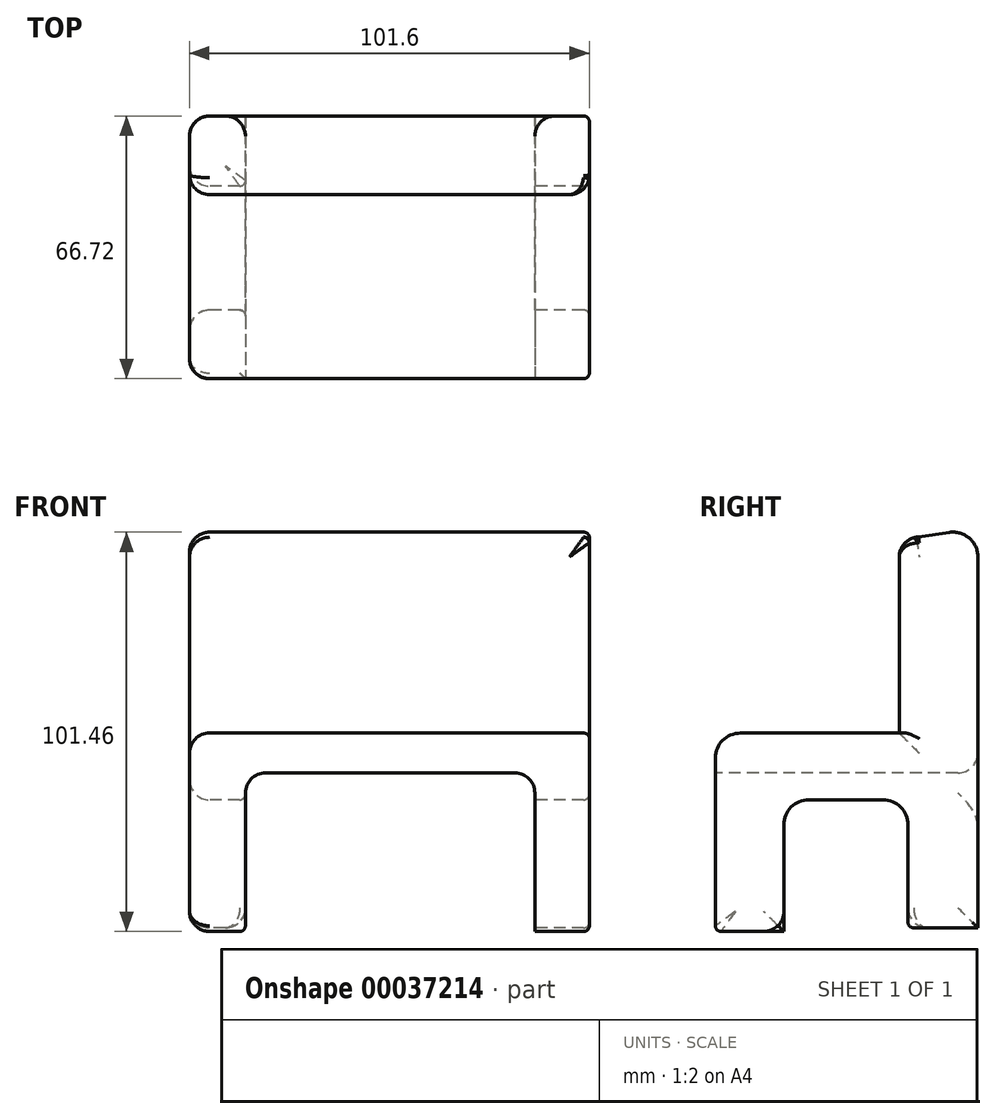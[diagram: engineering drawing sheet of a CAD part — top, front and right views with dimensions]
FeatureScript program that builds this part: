
annotation { "Feature Type Name" : "Feature", "Feature Type Description" : "" }
export const myFeature = defineFeature(function(context is Context, id is Id, definition is map)
    precondition{}
    {
        {
            var Q0;
            Q0=qCreatedBy(makeId("Right.planeOp"),FACE);
            var sketch = newSketch(context, id + "F0", { "sketchPlane" : qUnion([Q0])});
            skLineSegment(sketch, "E0", {"start": v(55.36, 61.66) * mm, "end": v(55.36, 14.39) * mm});
            skLineSegment(sketch, "E1", {"start": v(55.36, 14.39) * mm, "end": v(55.36, -32.54) * mm});
            skLineSegment(sketch, "E2", {"start": v(55.36, -32.54) * mm, "end": v(37.58, -32.54) * mm});
            skLineSegment(sketch, "E3", {"start": v(37.58, -32.54) * mm, "end": v(37.58, -6.35) * mm});
            skLineSegment(sketch, "E4", {"start": v(31.23, 0) * mm, "end": v(12.4, 0) * mm});
            skLineSegment(sketch, "E5", {"start": v(6.05, -6.35) * mm, "end": v(6.05, -33.45) * mm});
            skLineSegment(sketch, "E6", {"start": v(6.05, -33.45) * mm, "end": v(-11.36, -33.45) * mm});
            skLineSegment(sketch, "E7", {"start": v(-11.36, -33.45) * mm, "end": v(-11.36, 0) * mm});
            skLineSegment(sketch, "E8", {"start": v(-11.36, 0) * mm, "end": v(-11.36, 10.6) * mm});
            skLineSegment(sketch, "E9", {"start": v(-5.01, 16.96) * mm, "end": v(35.38, 16.96) * mm});
            skLineSegment(sketch, "E10", {"start": v(35.38, 16.96) * mm, "end": v(35.38, 66.08) * mm});
            skLineSegment(sketch, "E11", {"start": v(35.38, 66.08) * mm, "end": v(48.08, 67.94) * mm});
            skPoint(sketch, "E12.visualSharp", {"position": v(55.36, 69.01) * mm});
            skArc(sketch, "E12.filletArc", {"start": v(55.36, 61.66) * mm, "mid": v(53.16, 66.47) * mm, "end": v(48.08, 67.94) * mm});
            skPoint(sketch, "E13.visualSharp", {"position": v(-11.36, 16.96) * mm});
            skArc(sketch, "E13.filletArc", {"start": v(-5.01, 16.96) * mm, "mid": v(-9.5, 15.1) * mm, "end": v(-11.36, 10.6) * mm});
            skPoint(sketch, "E14.visualSharp", {"position": v(6.05, 0) * mm});
            skArc(sketch, "E14.filletArc", {"start": v(12.4, 0) * mm, "mid": v(7.9, -1.86) * mm, "end": v(6.05, -6.35) * mm});
            skPoint(sketch, "E15.visualSharp", {"position": v(37.58, 0) * mm});
            skArc(sketch, "E15.filletArc", {"start": v(37.58, -6.35) * mm, "mid": v(35.72, -1.86) * mm, "end": v(31.23, 0) * mm});
            skSolve(sketch);
        }
        {
            var Q0;
            Q0=makeQuery(id+"F0.imprint","IMPRINT",FACE,{"disambiguationData":[TD([[makeQuery(id+"F0.imprint","IMPRINT",EDGE,{"derivedFrom":sQuery(id+"F0.wireOp",EDGE,"E0")}),-1.0]])]});
            extrude(context, id + "F1", {"entities" : qUnion([Q0]), "depth" : 101.6 * mm});
        }
        {
            var Q0;
            Q0=makeQuery(id+"F1.opExtrude","SWEPT_FACE",FACE,{"disambiguationData":[OSD([sQuery(id+"F0.wireOp",EDGE,"E7"),sQuery(id+"F0.wireOp",EDGE,"E8")])]});
            var sketch = newSketch(context, id + "F2", { "sketchPlane" : qUnion([Q0])});
            skLineSegment(sketch, "E16.bottom", {"start": v(14.22, 6.83) * mm, "end": v(87.74, 6.83) * mm});
            skLineSegment(sketch, "E16.top", {"start": v(14.22, -33.45) * mm, "end": v(87.74, -33.45) * mm});
            skLineSegment(sketch, "E16.left", {"start": v(14.22, 6.83) * mm, "end": v(14.22, -33.45) * mm});
            skLineSegment(sketch, "E16.right", {"start": v(87.74, 6.83) * mm, "end": v(87.74, -33.45) * mm});
            skSolve(sketch);
        }
        {
            var Q0;
            Q0=makeQuery(id+"F2.imprint","IMPRINT",FACE,{"disambiguationData":[TD([[makeQuery(id+"F2.imprint","IMPRINT",EDGE,{"derivedFrom":sQuery(id+"F2.wireOp",EDGE,"E16.bottom")}),-1.0]])]});
            extrude(context, id + "F3", {"entities" : qUnion([Q0]), "operationType" : NewBodyOperationType.REMOVE, "oppositeDirection" : true, "depth" : 101.6 * mm});
        }
        {
            var Q0;
            Q0=makeQuery(id+"F1.opExtrude","CAP_FACE",FACE,{"disambiguationData":[OSD([sQuery(id+"F0.wireOp",EDGE,"E0"),sQuery(id+"F0.wireOp",EDGE,"E1"),sQuery(id+"F0.wireOp",EDGE,"E2"),sQuery(id+"F0.wireOp",EDGE,"E3"),sQuery(id+"F0.wireOp",EDGE,"E4"),sQuery(id+"F0.wireOp",EDGE,"E5"),sQuery(id+"F0.wireOp",EDGE,"E6"),sQuery(id+"F0.wireOp",EDGE,"E7"),sQuery(id+"F0.wireOp",EDGE,"E8"),sQuery(id+"F0.wireOp",EDGE,"E9"),sQuery(id+"F0.wireOp",EDGE,"E10"),sQuery(id+"F0.wireOp",EDGE,"E11"),sQuery(id+"F0.wireOp",EDGE,"E12.filletArc"),sQuery(id+"F0.wireOp",EDGE,"E13.filletArc"),sQuery(id+"F0.wireOp",EDGE,"E14.filletArc"),sQuery(id+"F0.wireOp",EDGE,"E15.filletArc")])],"isStart":true});
            fillet(context, id + "F4", {"entities" : qUnion([Q0]), "radius" : 5.08 * mm, "tangentPropagation" : true, "allowEdgeOverflow" : false});
        }
        {
            var Q0;
            Q0=makeQuery(id+"F3.boolean.opBoolean","COPY",EDGE,{"derivedFrom":makeQuery(id+"F3.opExtrude","CAP_EDGE",EDGE,{"disambiguationData":[OSD([sQuery(id+"F2.wireOp",EDGE,"E16.left")])],"isStart":true})});
            var Q1;
            Q1=makeQuery(id+"F3.boolean.opBoolean","COPY",EDGE,{"derivedFrom":makeQuery(id+"F3.opExtrude","CAP_EDGE",EDGE,{"disambiguationData":[OSD([sQuery(id+"F2.wireOp",EDGE,"E16.bottom")])],"isStart":true})});
            var Q2;
            Q2=makeQuery(id+"F3.boolean.opBoolean","INTERSECT",EDGE,{"derivedFrom":[makeQuery(id+"F1.opExtrude","SWEPT_FACE",FACE,{"disambiguationData":[OSD([sQuery(id+"F0.wireOp",EDGE,"E5")])]}),makeQuery(id+"F3.opExtrude","SWEPT_FACE",FACE,{"disambiguationData":[OSD([sQuery(id+"F2.wireOp",EDGE,"E16.left")])]})]});
            var Q3;
            Q3=makeQuery(id+"F3.boolean.opBoolean","COPY",EDGE,{"derivedFrom":makeQuery(id+"F3.opExtrude","SWEPT_EDGE",EDGE,{"disambiguationData":[OSD([sQuery(id+"F0.wireOp",EDGE,"E6"),sQuery(id+"F0.wireOp",EDGE,"E7"),sQuery(id+"F2.wireOp",EDGE,"E16.top"),sQuery(id+"F2.wireOp",EDGE,"E16.left")])]})});
            var Q4;
            {var subQ0=sQuery(id+"F0.wireOp",EDGE,"E6");var subQ1=sQuery(id+"F0.wireOp",EDGE,"E7");Q4=makeQuery(id+"F3.boolean.opBoolean","SPLIT",EDGE,{"disambiguationData":[TD([makeQuery(id+"F3.opExtrude","SWEPT_FACE",FACE,{"disambiguationData":[OSD([sQuery(id+"F2.wireOp",EDGE,"E16.left")])]})])],"derivedFrom":makeQuery(id+"F1.opExtrude","SWEPT_EDGE",EDGE,{"disambiguationData":[OSD([subQ0,subQ1])]})});}
            var Q5;
            {var subQ0=sQuery(id+"F0.wireOp",EDGE,"E6");var subQ1=sQuery(id+"F0.wireOp",EDGE,"E7");Q5=makeQuery(id+"F3.boolean.opBoolean","SPLIT",EDGE,{"disambiguationData":[TD([makeQuery(id+"F3.opExtrude","SWEPT_FACE",FACE,{"disambiguationData":[OSD([sQuery(id+"F2.wireOp",EDGE,"E16.right")])]})])],"derivedFrom":makeQuery(id+"F1.opExtrude","SWEPT_EDGE",EDGE,{"disambiguationData":[OSD([subQ0,subQ1])]})});}
            var Q6;
            Q6=makeQuery(id+"F1.opExtrude","CAP_EDGE",EDGE,{"disambiguationData":[OSD([sQuery(id+"F0.wireOp",EDGE,"E6")])],"isStart":false});
            var Q7;
            Q7=makeQuery(id+"F1.opExtrude","CAP_EDGE",EDGE,{"disambiguationData":[OSD([sQuery(id+"F0.wireOp",EDGE,"E7"),sQuery(id+"F0.wireOp",EDGE,"E8")])],"isStart":false});
            var Q8;
            Q8=makeQuery(id+"F3.boolean.opBoolean","COPY",EDGE,{"derivedFrom":makeQuery(id+"F3.opExtrude","CAP_EDGE",EDGE,{"disambiguationData":[OSD([sQuery(id+"F2.wireOp",EDGE,"E16.right")])],"isStart":true})});
            var Q9;
            Q9=makeQuery(id+"F1.opExtrude","CAP_EDGE",EDGE,{"disambiguationData":[OSD([sQuery(id+"F0.wireOp",EDGE,"E14.filletArc")])],"isStart":false});
            var Q10;
            Q10=makeQuery(id+"F1.opExtrude","CAP_EDGE",EDGE,{"disambiguationData":[OSD([sQuery(id+"F0.wireOp",EDGE,"E5")])],"isStart":false});
            var Q11;
            Q11=makeQuery(id+"F1.opExtrude","CAP_EDGE",EDGE,{"disambiguationData":[OSD([sQuery(id+"F0.wireOp",EDGE,"E4")])],"isStart":false});
            var Q12;
            Q12=makeQuery(id+"F1.opExtrude","CAP_EDGE",EDGE,{"disambiguationData":[OSD([sQuery(id+"F0.wireOp",EDGE,"E15.filletArc")])],"isStart":false});
            var Q13;
            Q13=makeQuery(id+"F1.opExtrude","CAP_EDGE",EDGE,{"disambiguationData":[OSD([sQuery(id+"F0.wireOp",EDGE,"E3")])],"isStart":false});
            var Q14;
            Q14=makeQuery(id+"F1.opExtrude","CAP_EDGE",EDGE,{"disambiguationData":[OSD([sQuery(id+"F0.wireOp",EDGE,"E2")])],"isStart":false});
            var Q15;
            {var subQ0=sQuery(id+"F0.wireOp",EDGE,"E2");var subQ1=sQuery(id+"F0.wireOp",EDGE,"E3");Q15=makeQuery(id+"F3.boolean.opBoolean","SPLIT",EDGE,{"disambiguationData":[TD([makeQuery(id+"F3.opExtrude","SWEPT_FACE",FACE,{"disambiguationData":[OSD([sQuery(id+"F2.wireOp",EDGE,"E16.right")])]})])],"derivedFrom":makeQuery(id+"F1.opExtrude","SWEPT_EDGE",EDGE,{"disambiguationData":[OSD([subQ0,subQ1])]})});}
            var Q16;
            Q16=makeQuery(id+"F1.opExtrude","CAP_EDGE",EDGE,{"disambiguationData":[OSD([sQuery(id+"F0.wireOp",EDGE,"E0"),sQuery(id+"F0.wireOp",EDGE,"E1")])],"isStart":false});
            fillet(context, id + "F5", {"entities" : qUnion([Q0, Q1, Q2, Q3, Q4, Q5, Q6, Q7, Q8, Q9, Q10, Q11, Q12, Q13, Q14, Q15, Q16]), "radius" : 1.45 * mm, "tangentPropagation" : true, "allowEdgeOverflow" : false});
        }
        {
            var Q0;
            Q0=makeQuery(id+"F1.opExtrude","CAP_EDGE",EDGE,{"disambiguationData":[OSD([sQuery(id+"F0.wireOp",EDGE,"E10")])],"isStart":false});
            var Q1;
            Q1=makeQuery(id+"F1.opExtrude","SWEPT_EDGE",EDGE,{"disambiguationData":[OSD([sQuery(id+"F0.wireOp",EDGE,"E10"),sQuery(id+"F0.wireOp",EDGE,"E11")])]});
            var Q2;
            {var subQ0=sQuery(id+"F0.wireOp",EDGE,"E6");Q2=makeQuery(id+"F5.opFillet","BLEND_EDGE",EDGE,{"blendedFrom":[makeQuery(id+"F1.opExtrude","CAP_EDGE",EDGE,{"disambiguationData":[OSD([subQ0])],"isStart":false}),makeQuery(id+"F1.opExtrude","CAP_FACE",FACE,{"disambiguationData":[OSD([sQuery(id+"F0.wireOp",EDGE,"E0"),sQuery(id+"F0.wireOp",EDGE,"E1"),sQuery(id+"F0.wireOp",EDGE,"E2"),sQuery(id+"F0.wireOp",EDGE,"E3"),sQuery(id+"F0.wireOp",EDGE,"E4"),sQuery(id+"F0.wireOp",EDGE,"E5"),subQ0,sQuery(id+"F0.wireOp",EDGE,"E7"),sQuery(id+"F0.wireOp",EDGE,"E8"),sQuery(id+"F0.wireOp",EDGE,"E9"),sQuery(id+"F0.wireOp",EDGE,"E10"),sQuery(id+"F0.wireOp",EDGE,"E11"),sQuery(id+"F0.wireOp",EDGE,"E12.filletArc"),sQuery(id+"F0.wireOp",EDGE,"E13.filletArc"),sQuery(id+"F0.wireOp",EDGE,"E14.filletArc"),sQuery(id+"F0.wireOp",EDGE,"E15.filletArc")])],"isStart":false})],"blendedInto":[makeQuery(id+"F1.opExtrude","CAP_FACE",FACE,{"disambiguationData":[OSD([sQuery(id+"F0.wireOp",EDGE,"E0"),sQuery(id+"F0.wireOp",EDGE,"E1"),sQuery(id+"F0.wireOp",EDGE,"E2"),sQuery(id+"F0.wireOp",EDGE,"E3"),sQuery(id+"F0.wireOp",EDGE,"E4"),sQuery(id+"F0.wireOp",EDGE,"E5"),subQ0,sQuery(id+"F0.wireOp",EDGE,"E7"),sQuery(id+"F0.wireOp",EDGE,"E8"),sQuery(id+"F0.wireOp",EDGE,"E9"),sQuery(id+"F0.wireOp",EDGE,"E10"),sQuery(id+"F0.wireOp",EDGE,"E11"),sQuery(id+"F0.wireOp",EDGE,"E12.filletArc"),sQuery(id+"F0.wireOp",EDGE,"E13.filletArc"),sQuery(id+"F0.wireOp",EDGE,"E14.filletArc"),sQuery(id+"F0.wireOp",EDGE,"E15.filletArc")])],"isStart":false})]});}
            var Q3;
            {var subQ0=sQuery(id+"F0.wireOp",EDGE,"E5");Q3=makeQuery(id+"F5.opFillet","BLEND_EDGE",EDGE,{"blendedFrom":[makeQuery(id+"F1.opExtrude","CAP_EDGE",EDGE,{"disambiguationData":[OSD([subQ0])],"isStart":false}),makeQuery(id+"F1.opExtrude","CAP_FACE",FACE,{"disambiguationData":[OSD([sQuery(id+"F0.wireOp",EDGE,"E0"),sQuery(id+"F0.wireOp",EDGE,"E1"),sQuery(id+"F0.wireOp",EDGE,"E2"),sQuery(id+"F0.wireOp",EDGE,"E3"),sQuery(id+"F0.wireOp",EDGE,"E4"),subQ0,sQuery(id+"F0.wireOp",EDGE,"E6"),sQuery(id+"F0.wireOp",EDGE,"E7"),sQuery(id+"F0.wireOp",EDGE,"E8"),sQuery(id+"F0.wireOp",EDGE,"E9"),sQuery(id+"F0.wireOp",EDGE,"E10"),sQuery(id+"F0.wireOp",EDGE,"E11"),sQuery(id+"F0.wireOp",EDGE,"E12.filletArc"),sQuery(id+"F0.wireOp",EDGE,"E13.filletArc"),sQuery(id+"F0.wireOp",EDGE,"E14.filletArc"),sQuery(id+"F0.wireOp",EDGE,"E15.filletArc")])],"isStart":false})],"blendedInto":[makeQuery(id+"F1.opExtrude","CAP_FACE",FACE,{"disambiguationData":[OSD([sQuery(id+"F0.wireOp",EDGE,"E0"),sQuery(id+"F0.wireOp",EDGE,"E1"),sQuery(id+"F0.wireOp",EDGE,"E2"),sQuery(id+"F0.wireOp",EDGE,"E3"),sQuery(id+"F0.wireOp",EDGE,"E4"),subQ0,sQuery(id+"F0.wireOp",EDGE,"E6"),sQuery(id+"F0.wireOp",EDGE,"E7"),sQuery(id+"F0.wireOp",EDGE,"E8"),sQuery(id+"F0.wireOp",EDGE,"E9"),sQuery(id+"F0.wireOp",EDGE,"E10"),sQuery(id+"F0.wireOp",EDGE,"E11"),sQuery(id+"F0.wireOp",EDGE,"E12.filletArc"),sQuery(id+"F0.wireOp",EDGE,"E13.filletArc"),sQuery(id+"F0.wireOp",EDGE,"E14.filletArc"),sQuery(id+"F0.wireOp",EDGE,"E15.filletArc")])],"isStart":false})]});}
            var Q4;
            {var subQ0=sQuery(id+"F0.wireOp",EDGE,"E15.filletArc");Q4=makeQuery(id+"F5.opFillet","BLEND_EDGE",EDGE,{"blendedFrom":[makeQuery(id+"F1.opExtrude","CAP_EDGE",EDGE,{"disambiguationData":[OSD([subQ0])],"isStart":false}),makeQuery(id+"F3.boolean.opBoolean","SPLIT",FACE,{"disambiguationData":[TD([makeQuery(id+"F3.opExtrude","SWEPT_FACE",FACE,{"disambiguationData":[OSD([sQuery(id+"F2.wireOp",EDGE,"E16.right")])]})])],"derivedFrom":makeQuery(id+"F1.opExtrude","SWEPT_FACE",FACE,{"disambiguationData":[OSD([subQ0])]})})],"blendedInto":[makeQuery(id+"F3.boolean.opBoolean","SPLIT",FACE,{"disambiguationData":[TD([makeQuery(id+"F3.opExtrude","SWEPT_FACE",FACE,{"disambiguationData":[OSD([sQuery(id+"F2.wireOp",EDGE,"E16.right")])]})])],"derivedFrom":makeQuery(id+"F1.opExtrude","SWEPT_FACE",FACE,{"disambiguationData":[OSD([subQ0])]})})]});}
            var Q5;
            {var subQ0=sQuery(id+"F0.wireOp",EDGE,"E2");var subQ1=sQuery(id+"F0.wireOp",EDGE,"E3");var subQ2=makeQuery(id+"F3.opExtrude","SWEPT_FACE",FACE,{"disambiguationData":[OSD([sQuery(id+"F2.wireOp",EDGE,"E16.right")])]});var subQ3=makeQuery(id+"F1.opExtrude","SWEPT_FACE",FACE,{"disambiguationData":[OSD([subQ1])]});Q5=makeQuery(id+"F5.opFillet","BLEND_EDGE",EDGE,{"blendedFrom":[makeQuery(id+"F3.boolean.opBoolean","SPLIT",EDGE,{"disambiguationData":[TD([subQ2])],"derivedFrom":makeQuery(id+"F1.opExtrude","SWEPT_EDGE",EDGE,{"disambiguationData":[OSD([subQ0,subQ1])]})}),makeQuery(id+"F3.boolean.opBoolean","SPLIT",FACE,{"disambiguationData":[TD([subQ2])],"derivedFrom":subQ3})],"blendedInto":[makeQuery(id+"F3.boolean.opBoolean","SPLIT",FACE,{"disambiguationData":[TD([subQ2])],"derivedFrom":subQ3})]});}
            var Q6;
            {var subQ0=sQuery(id+"F2.wireOp",EDGE,"E16.left");Q6=makeQuery(id+"F5.opFillet","BLEND_EDGE",EDGE,{"blendedFrom":[makeQuery(id+"F3.boolean.opBoolean","COPY",EDGE,{"derivedFrom":makeQuery(id+"F3.opExtrude","SWEPT_EDGE",EDGE,{"disambiguationData":[OSD([sQuery(id+"F0.wireOp",EDGE,"E6"),sQuery(id+"F0.wireOp",EDGE,"E7"),sQuery(id+"F2.wireOp",EDGE,"E16.top"),subQ0])]})}),makeQuery(id+"F3.boolean.opBoolean","COPY",FACE,{"derivedFrom":makeQuery(id+"F3.opExtrude","SWEPT_FACE",FACE,{"disambiguationData":[OSD([subQ0])]})})],"blendedInto":[makeQuery(id+"F3.boolean.opBoolean","COPY",FACE,{"derivedFrom":makeQuery(id+"F3.opExtrude","SWEPT_FACE",FACE,{"disambiguationData":[OSD([subQ0])]})})]});}
            var Q7;
            {var subQ0=sQuery(id+"F0.wireOp",EDGE,"E2");var subQ1=sQuery(id+"F0.wireOp",EDGE,"E3");Q7=makeQuery(id+"F3.boolean.opBoolean","SPLIT",EDGE,{"disambiguationData":[TD([makeQuery(id+"F3.opExtrude","SWEPT_FACE",FACE,{"disambiguationData":[OSD([sQuery(id+"F2.wireOp",EDGE,"E16.left")])]})])],"derivedFrom":makeQuery(id+"F1.opExtrude","SWEPT_EDGE",EDGE,{"disambiguationData":[OSD([subQ0,subQ1])]})});}
            var Q8;
            {var subQ0=sQuery(id+"F0.wireOp",EDGE,"E5");var subQ1=sQuery(id+"F0.wireOp",EDGE,"E6");Q8=makeQuery(id+"F3.boolean.opBoolean","SPLIT",EDGE,{"disambiguationData":[TD([makeQuery(id+"F3.opExtrude","SWEPT_FACE",FACE,{"disambiguationData":[OSD([sQuery(id+"F2.wireOp",EDGE,"E16.right")])]})])],"derivedFrom":makeQuery(id+"F1.opExtrude","SWEPT_EDGE",EDGE,{"disambiguationData":[OSD([subQ0,subQ1])]})});}
            var Q9;
            {var subQ0=sQuery(id+"F2.wireOp",EDGE,"E16.bottom");Q9=makeQuery(id+"F5.opFillet","BLEND_EDGE",EDGE,{"blendedFrom":[makeQuery(id+"F3.boolean.opBoolean","COPY",EDGE,{"derivedFrom":makeQuery(id+"F3.opExtrude","CAP_EDGE",EDGE,{"disambiguationData":[OSD([subQ0])],"isStart":true})}),makeQuery(id+"F3.boolean.opBoolean","COPY",FACE,{"derivedFrom":makeQuery(id+"F3.opExtrude","SWEPT_FACE",FACE,{"disambiguationData":[OSD([subQ0])]})})],"blendedInto":[makeQuery(id+"F3.boolean.opBoolean","COPY",FACE,{"derivedFrom":makeQuery(id+"F3.opExtrude","SWEPT_FACE",FACE,{"disambiguationData":[OSD([subQ0])]})})]});}
            var Q10;
            Q10=makeQuery(id+"F3.boolean.opBoolean","INTERSECT",EDGE,{"derivedFrom":[makeQuery(id+"F1.opExtrude","SWEPT_FACE",FACE,{"disambiguationData":[OSD([sQuery(id+"F0.wireOp",EDGE,"E0"),sQuery(id+"F0.wireOp",EDGE,"E1")])]}),makeQuery(id+"F3.opExtrude","SWEPT_FACE",FACE,{"disambiguationData":[OSD([sQuery(id+"F2.wireOp",EDGE,"E16.bottom")])]})]});
            var Q11;
            Q11=makeQuery(id+"F3.boolean.opBoolean","COPY",EDGE,{"derivedFrom":makeQuery(id+"F3.opExtrude","SWEPT_EDGE",EDGE,{"disambiguationData":[OSD([sQuery(id+"F2.wireOp",EDGE,"E16.bottom"),sQuery(id+"F2.wireOp",EDGE,"E16.left")])]})});
            var Q12;
            Q12=makeQuery(id+"F3.boolean.opBoolean","COPY",EDGE,{"derivedFrom":makeQuery(id+"F3.opExtrude","SWEPT_EDGE",EDGE,{"disambiguationData":[OSD([sQuery(id+"F2.wireOp",EDGE,"E16.bottom"),sQuery(id+"F2.wireOp",EDGE,"E16.right")])]})});
            fillet(context, id + "F6", {"entities" : qUnion([Q0, Q1, Q2, Q3, Q4, Q5, Q6, Q7, Q8, Q9, Q10, Q11, Q12]), "radius" : 5.08 * mm, "tangentPropagation" : true, "allowEdgeOverflow" : false});
        }
    });
